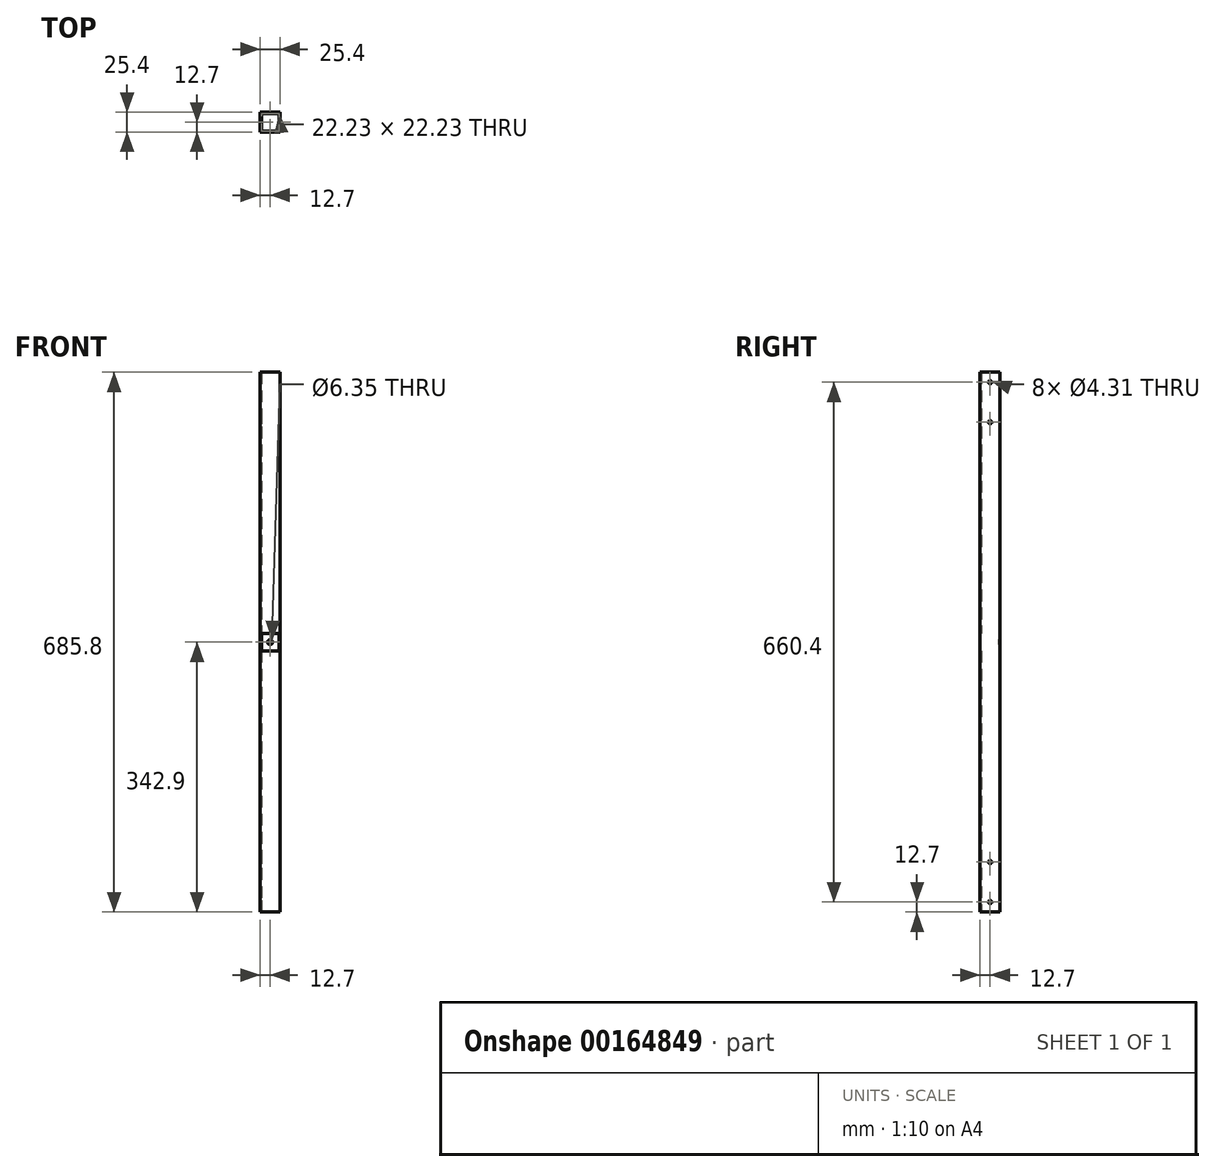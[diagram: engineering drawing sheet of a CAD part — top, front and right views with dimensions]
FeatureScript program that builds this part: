
annotation { "Feature Type Name" : "Feature", "Feature Type Description" : "" }
export const myFeature = defineFeature(function(context is Context, id is Id, definition is map)
    precondition{}
    {
        {
            var Q0;
            Q0=qCreatedBy(makeId("Top.planeOp"),FACE);
            var sketch = newSketch(context, id + "F0", { "sketchPlane" : qUnion([Q0])});
            skLineSegment(sketch, "E0.bottom", {"start": v(11.11, -11.11) * mm, "end": v(-11.11, -11.11) * mm});
            skLineSegment(sketch, "E0.top", {"start": v(11.11, 11.11) * mm, "end": v(-11.11, 11.11) * mm});
            skLineSegment(sketch, "E0.left", {"start": v(11.11, -11.11) * mm, "end": v(11.11, 11.11) * mm});
            skLineSegment(sketch, "E0.right", {"start": v(-11.11, -11.11) * mm, "end": v(-11.11, 11.11) * mm});
            skPoint(sketch, "E0.middle", {"position": v(0, 0) * mm});
            skLineSegment(sketch, "E1.bottom", {"start": v(12.7, -12.7) * mm, "end": v(-12.7, -12.7) * mm});
            skLineSegment(sketch, "E1.top", {"start": v(12.7, 12.7) * mm, "end": v(-12.7, 12.7) * mm});
            skLineSegment(sketch, "E1.left", {"start": v(12.7, -12.7) * mm, "end": v(12.7, 12.7) * mm});
            skLineSegment(sketch, "E1.right", {"start": v(-12.7, -12.7) * mm, "end": v(-12.7, 12.7) * mm});
            skSolve(sketch);
        }
        {
            var Q0;
            Q0=qSketchRegion(id+"F0",true);
            extrude(context, id + "F1", {"entities" : qUnion([Q0]), "depth" : 685.8 * mm});
        }
        {
            var Q0;
            Q0=qCreatedBy(makeId("Front.planeOp"),FACE);
            var sketch = newSketch(context, id + "F2", { "sketchPlane" : qUnion([Q0])});
            skLineSegment(sketch, "E2", {"start": v(0, 0) * mm, "end": v(0, 685.8) * mm, "construction": true});
            skLineSegment(sketch, "E3.bottom", {"start": v(-11.11, 331.79) * mm, "end": v(11.11, 331.79) * mm});
            skLineSegment(sketch, "E3.top", {"start": v(-11.11, 354.01) * mm, "end": v(11.11, 354.01) * mm});
            skLineSegment(sketch, "E3.left", {"start": v(-11.11, 331.79) * mm, "end": v(-11.11, 354.01) * mm});
            skLineSegment(sketch, "E3.right", {"start": v(11.11, 331.79) * mm, "end": v(11.11, 354.01) * mm});
            skPoint(sketch, "E3.middle", {"position": v(0, 342.9) * mm});
            skSolve(sketch);
        }
        {
            var Q0;
            Q0 = qSketchRegion(id + "F2", true);
            var Q1;
            Q1=makeQuery(id+"F1.opExtrude","SWEPT_FACE",FACE,{"disambiguationData":[OSD([sQuery(id+"F0.wireOp",EDGE,"E1.bottom")])]});
            extrude(context, id + "F3", {"entities" : qUnion([Q0]), "operationType" : NewBodyOperationType.REMOVE, "endBound" : BoundingType.UP_TO_SURFACE, "endBoundEntityFace" : qUnion([Q1]), "depth" : 25.4 * mm});
        }
        {
            var Q0;
            Q0=makeQuery(id+"F1.opExtrude","SWEPT_FACE",FACE,{"disambiguationData":[OSD([sQuery(id+"F0.wireOp",EDGE,"E1.top")])]});
            var sketch = newSketch(context, id + "F4", { "sketchPlane" : qUnion([Q0])});
            skLineSegment(sketch, "E4", {"start": v(12.7, 342.9) * mm, "end": v(-12.7, 342.9) * mm, "construction": true});
            skCircle(sketch, "E5", {"center": v(0, 342.9) * mm, "radius": 3.17 * mm});
            skSolve(sketch);
        }
        {
            var Q0;
            Q0 = qSketchRegion(id + "F4", true);
            var Q1;
            Q1=makeQuery(id+"F1.opExtrude","SWEPT_FACE",FACE,{"disambiguationData":[OSD([sQuery(id+"F0.wireOp",EDGE,"E0.top")])]});
            extrude(context, id + "F5", {"entities" : qUnion([Q0]), "operationType" : NewBodyOperationType.REMOVE, "endBound" : BoundingType.UP_TO_SURFACE, "oppositeDirection" : true, "endBoundEntityFace" : qUnion([Q1]), "depth" : 25.4 * mm});
        }
        {
            var Q0;
            Q0=makeQuery(id+"F1.opExtrude","SWEPT_FACE",FACE,{"disambiguationData":[OSD([sQuery(id+"F0.wireOp",EDGE,"E1.right")])]});
            var sketch = newSketch(context, id + "F6", { "sketchPlane" : qUnion([Q0])});
            skLineSegment(sketch, "E6.bottom", {"start": v(0, 0) * mm, "end": v(-12.7, 0) * mm, "construction": true});
            skLineSegment(sketch, "E6.top", {"start": v(0, 12.7) * mm, "end": v(-12.7, 12.7) * mm, "construction": true});
            skLineSegment(sketch, "E6.left", {"start": v(0, 0) * mm, "end": v(0, 12.7) * mm, "construction": true});
            skLineSegment(sketch, "E6.right", {"start": v(-12.7, 0) * mm, "end": v(-12.7, 12.7) * mm, "construction": true});
            skLineSegment(sketch, "E7.bottom", {"start": v(0, 685.8) * mm, "end": v(-12.7, 685.8) * mm, "construction": true});
            skLineSegment(sketch, "E7.top", {"start": v(0, 673.1) * mm, "end": v(-12.7, 673.1) * mm, "construction": true});
            skLineSegment(sketch, "E7.left", {"start": v(0, 685.8) * mm, "end": v(0, 673.1) * mm, "construction": true});
            skLineSegment(sketch, "E7.right", {"start": v(-12.7, 685.8) * mm, "end": v(-12.7, 673.1) * mm, "construction": true});
            skLineSegment(sketch, "E8", {"start": v(0, 12.7) * mm, "end": v(0, 63.5) * mm, "construction": true});
            skLineSegment(sketch, "E9", {"start": v(0, 673.1) * mm, "end": v(0, 622.3) * mm, "construction": true});
            skCircle(sketch, "E10", {"center": v(0, 12.7) * mm, "radius": 2.15 * mm});
            skCircle(sketch, "E11", {"center": v(0, 63.5) * mm, "radius": 2.15 * mm});
            skCircle(sketch, "E12", {"center": v(0, 673.1) * mm, "radius": 2.15 * mm});
            skCircle(sketch, "E13", {"center": v(0, 622.3) * mm, "radius": 2.15 * mm});
            skSolve(sketch);
        }
        {
            var Q0;
            Q0 = qSketchRegion(id + "F6", true);
            var Q1;
            Q1=makeQuery(id+"F1.opExtrude","SWEPT_FACE",FACE,{"disambiguationData":[OSD([sQuery(id+"F0.wireOp",EDGE,"E1.left")])]});
            extrude(context, id + "F7", {"entities" : qUnion([Q0]), "operationType" : NewBodyOperationType.REMOVE, "endBound" : BoundingType.UP_TO_SURFACE, "oppositeDirection" : true, "endBoundEntityFace" : qUnion([Q1]), "depth" : 25.4 * mm});
        }
    });
